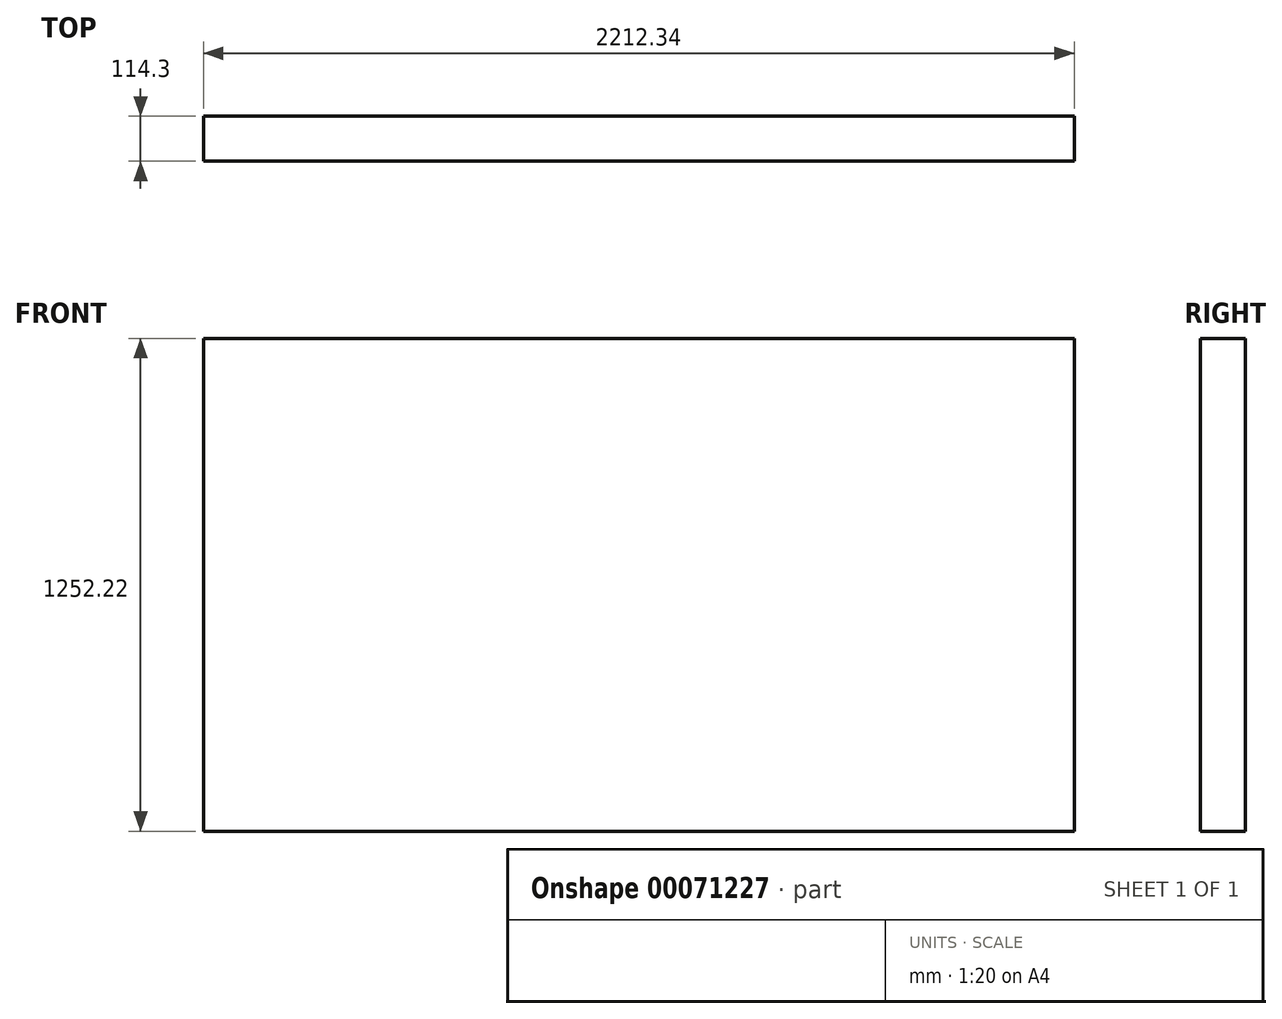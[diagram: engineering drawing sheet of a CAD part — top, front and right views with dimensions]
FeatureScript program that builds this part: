
annotation { "Feature Type Name" : "Feature", "Feature Type Description" : "" }
export const myFeature = defineFeature(function(context is Context, id is Id, definition is map)
    precondition{}
    {
        {
            var Q0;
            Q0=qCreatedBy(makeId("Front.planeOp"),FACE);
            var sketch = newSketch(context, id + "F0", { "sketchPlane" : qUnion([Q0])});
            skLineSegment(sketch, "E0.bottom", {"start": v(-1105.83, 1164.38) * mm, "end": v(1106.5, 1164.38) * mm});
            skLineSegment(sketch, "E0.top", {"start": v(-1105.83, -87.84) * mm, "end": v(1106.5, -87.84) * mm});
            skLineSegment(sketch, "E0.left", {"start": v(-1105.83, 1164.38) * mm, "end": v(-1105.83, -87.84) * mm});
            skLineSegment(sketch, "E0.right", {"start": v(1106.5, 1164.38) * mm, "end": v(1106.5, -87.84) * mm});
            skSolve(sketch);
        }
        {
            var Q0;
            Q0=makeQuery(id+"F0.imprint","IMPRINT",FACE,{"disambiguationData":[TD([[makeQuery(id+"F0.imprint","IMPRINT",EDGE,{"derivedFrom":sQuery(id+"F0.wireOp",EDGE,"E0.bottom")}),-1.0]])]});
            extrude(context, id + "F1", {"entities" : qUnion([Q0]), "depth" : 114.3 * mm});
        }
    });
